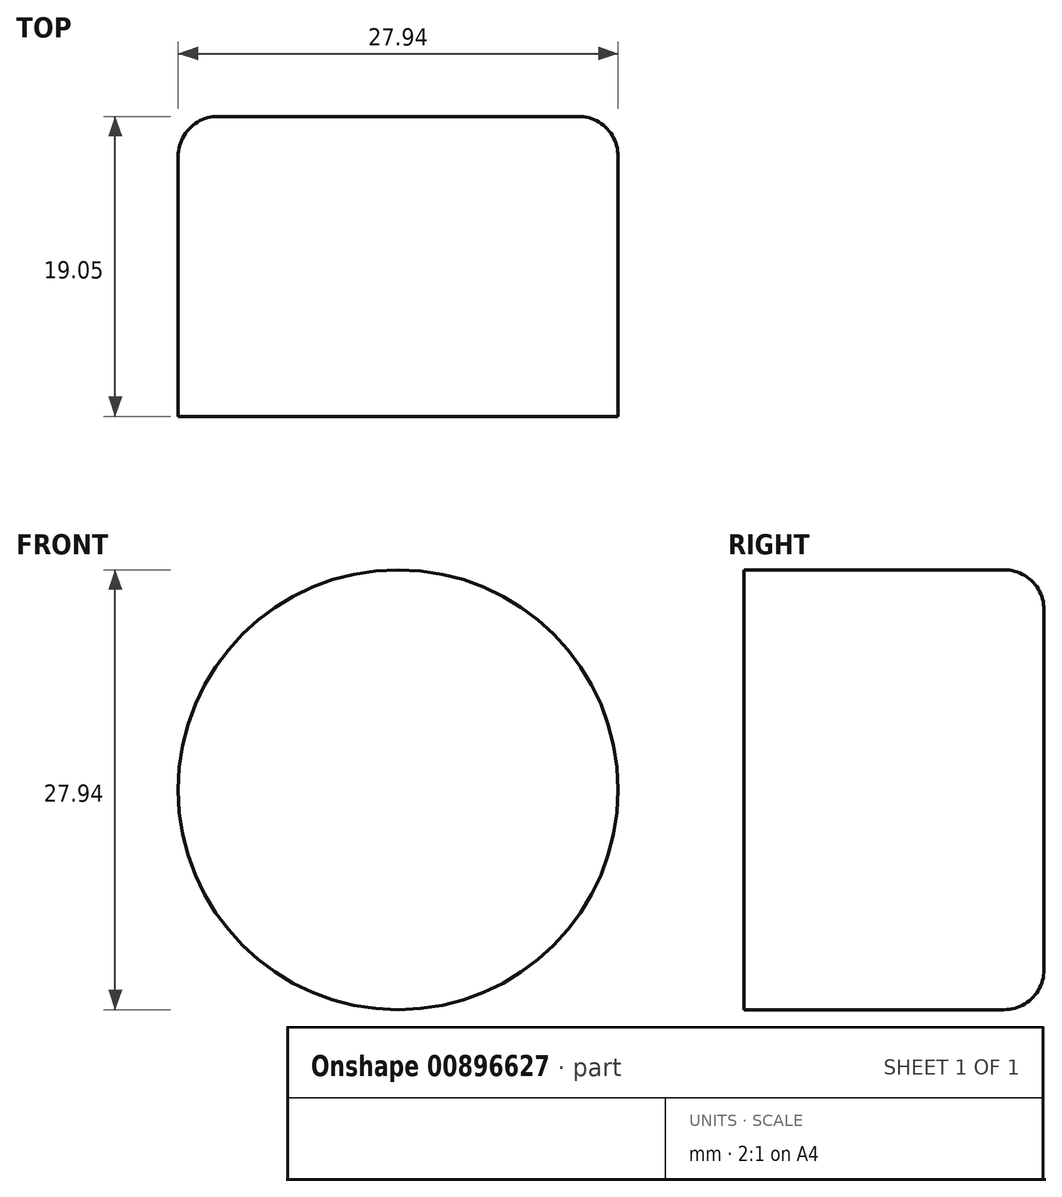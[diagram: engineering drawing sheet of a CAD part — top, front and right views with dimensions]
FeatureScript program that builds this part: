
annotation { "Feature Type Name" : "Feature", "Feature Type Description" : "" }
export const myFeature = defineFeature(function(context is Context, id is Id, definition is map)
    precondition{}
    {
        {
            var Q0;
            Q0=qCreatedBy(makeId("Front.planeOp"),FACE);
            var sketch = newSketch(context, id + "F0", { "sketchPlane" : qUnion([Q0])});
            skCircle(sketch, "E0", {"center": v(-63.36, 0) * mm, "radius": 13.97 * mm});
            skSolve(sketch);
        }
        {
            var Q0;
            Q0=makeQuery(id+"F0.imprint","IMPRINT",FACE,{"disambiguationData":[TD([[makeQuery(id+"F0.imprint","IMPRINT",EDGE,{"derivedFrom":sQuery(id+"F0.wireOp",EDGE,"woK1bgaw-g6SX-4bgO-quy7-SqlsBxIy7Zxn")}),1.0]])]});
            var Q1;
            Q1=makeQuery(id+"F0.imprint","IMPRINT",FACE,{"disambiguationData":[TD([[makeQuery(id+"F0.imprint","IMPRINT",EDGE,{"derivedFrom":sQuery(id+"F0.wireOp",EDGE,"E0")}),1.0]])]});
            extrude(context, id + "F1", {"entities" : qUnion([Q0, Q1]), "oppositeDirection" : true, "depth" : 19.05 * mm, "offsetDistance" : 25.4 * mm});
        }
        {
            var Q0;
            Q0=makeQuery(id+"F1.opExtrude","CAP_FACE",FACE,{"disambiguationData":[OSD([sQuery(id+"F0.wireOp",EDGE,"E0")])],"isStart":false});
            fillet(context, id + "F2", {"entities" : qUnion([Q0]), "radius" : 2.54 * mm, "tangentPropagation" : true, "defaultsChanged" : false, "vertexSettings" : [], "allowEdgeOverflow" : false});
        }
        {
            var Q0;
            Q0=makeQuery(id+"F1.opExtrude","SWEPT_BODY",BODY,{"disambiguationData":[OSD([sQuery(id+"F0.wireOp",EDGE,"woK1bgaw-g6SX-4bgO-quy7-SqlsBxIy7Zxn"),sQuery(id+"F0.wireOp",EDGE,"E0")])]});
            transform(context, id + "F3", {"entities" : qUnion([Q0]), "transformType" : TransformType.TRANSLATION_3D, "dx" : 65.8 * mm, "dy" : 0 * mm, "dz" : 0 * mm, "makeCopy" : false});
        }
    });
